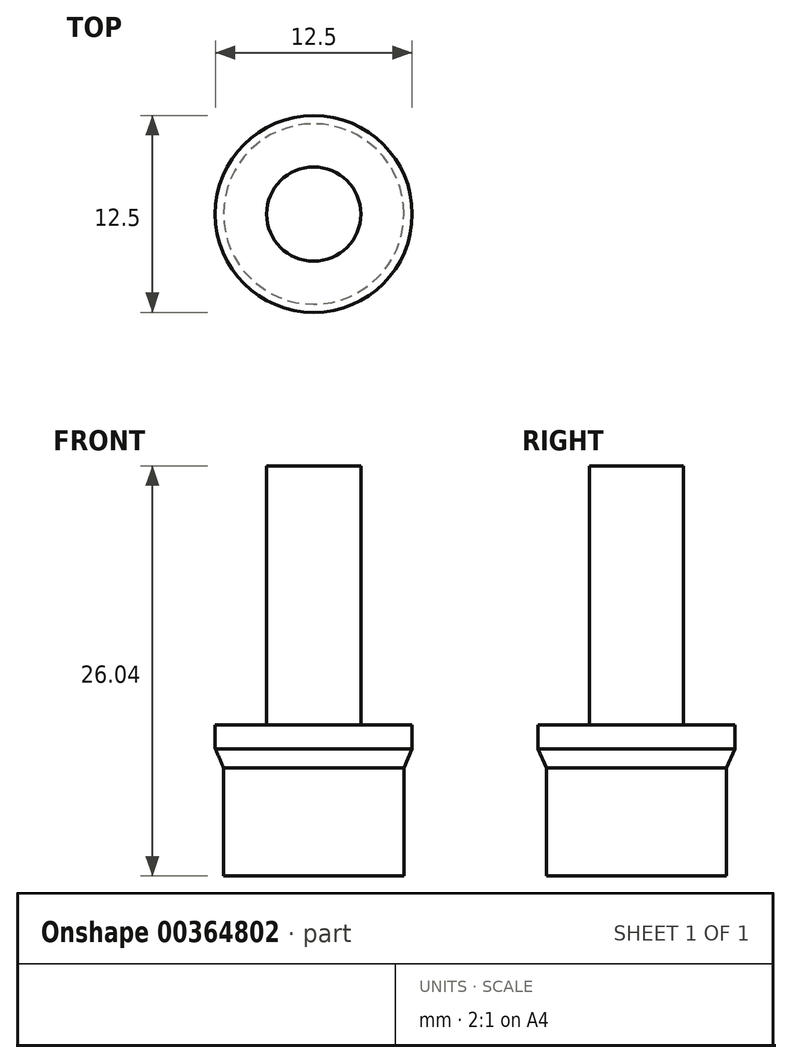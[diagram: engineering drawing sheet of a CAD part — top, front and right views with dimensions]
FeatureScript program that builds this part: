
annotation { "Feature Type Name" : "Feature", "Feature Type Description" : "" }
export const myFeature = defineFeature(function(context is Context, id is Id, definition is map)
    precondition{}
    {
        {
            var Q0;
            Q0=qCreatedBy(makeId("Front.planeOp"),FACE);
            var sketch = newSketch(context, id + "F0", { "sketchPlane" : qUnion([Q0])});
            skLineSegment(sketch, "E0", {"start": v(0, 0) * mm, "end": v(0, 26.04) * mm});
            skLineSegment(sketch, "E1", {"start": v(0, 0) * mm, "end": v(5.73, 0) * mm});
            skLineSegment(sketch, "E2", {"start": v(5.73, 0) * mm, "end": v(5.73, 6.87) * mm});
            skLineSegment(sketch, "E3", {"start": v(5.73, 6.87) * mm, "end": v(6.25, 8.08) * mm});
            skLineSegment(sketch, "E4", {"start": v(6.25, 8.08) * mm, "end": v(6.25, 9.58) * mm});
            skLineSegment(sketch, "E5", {"start": v(6.25, 9.58) * mm, "end": v(3, 9.58) * mm});
            skLineSegment(sketch, "E6", {"start": v(3, 9.58) * mm, "end": v(3, 26.04) * mm});
            skLineSegment(sketch, "E7", {"start": v(3, 26.04) * mm, "end": v(0, 26.04) * mm});
            skSolve(sketch);
        }
        {
            var Q0;
            Q0=makeQuery(id+"F0.imprint","IMPRINT",FACE,{"disambiguationData":[TD([[makeQuery(id+"F0.imprint","IMPRINT",EDGE,{"derivedFrom":sQuery(id+"F0.wireOp",EDGE,"E0")}),-1.0]])]});
            var Q1;
            Q1=sQuery(id+"F0.wireOp",EDGE,"E0");
            revolve(context, id + "F1", {"entities" : qUnion([Q0]), "axis" : qUnion([Q1]), "revolveType" : RevolveType.FULL});
        }
    });
